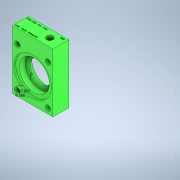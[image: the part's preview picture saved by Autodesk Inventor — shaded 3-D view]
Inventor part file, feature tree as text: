
AUTODESK INVENTOR PART (.ipt)
format: ipt  version: 2020 (Build 240168000, 168)  size: 548,352 bytes
history: native  units: in
note: dims shown in document units (in); Inventor stores cm internally (conversion verified against a paired STEP export)
features: sketch x5, hole x4, extrude x3, imported_body x1
ambient origin geometry x8: Origin, YZ Plane, XZ Plane, XY Plane, X Axis, Y Axis, Z Axis, Center Point
bodies: Solid1 (feature_tree)
feature tree (13):
  extrude  "Extrusion1"  Depth=0.3937in TaperAngle=0.0deg
  extrude  "Extrusion2"  Depth=0.3743in
  sketch  "Sketch3"  dims[d11=0.213in d12=0.2362in d13=0.4375in d14=0.25in d15=0.563in d16=0.375in d17=0.0in d18=0.3743in]
  hole  "Hole1"  [1 undecoded]
  hole  "Hole2"  [1 undecoded]
  sketch  "Sketch4"  dims[d19=0.0in]
  hole  "Hole3"  [1 undecoded]
  hole  "Hole4"  [1 undecoded]
  extrude  "Extrusion3"  [1 undecoded]
  sketch  "Sketch1"  dims[d0=0.6398in d1=0.0in d2=0.3937in d3=0.0in]
  sketch  "Sketch2"  dims[d4=0.04in d5=0.2362in d6=0.4375in d7=0.25in d8=0.563in d9=0.9843in d10=0.8108in]
  sketch  "Sketch5"  dims[d20=0.213in d21=0.2362in d22=0.4375in d23=0.25in d24=0.563in d25=0.375in d26=0.0in d27=0.04in d28=0.2362in d29=0.4375in d30=0.25in d31=0.563in d32=1.0in d33=0.8108in d34=0.1181in d35=0.0in]
  imported_body  "Base1"
note: 5 required parameter values undecoded (feature->parameter linkage not recoverable at this tier; creation-order binding heuristic only, values carry confidence <= 0.55)
